# Revit family: Термостатический клапан HERZ-TS-90-E повышенной пропускной способности, угловой 7724
name_source: partatom
category: Rohrzubehör
revit_build: Autodesk Revit 2018 (Build: 20190510_1515(x64)
units: mm (PartAtom-declared; Revit-internal decimal feet)

## family parameters
Arbeitsebenenbasiert = Nein
Beim Laden mit Abzugskörper schneiden = Nein
Bemaßung runder Anschluss = Durchmesser verwenden
Gemeinsam genutzt = Nein
Immer vertikal = Ja
OmniClass-Nummer = 23.65.55.14
OmniClass-Titel = Valves for Liquid Services
Teiletyp = Unterbricht

## types (16) — shared parameters
H04 = 4.5 mm  [stored 0.0147638 ft]
H06 = 17 mm
H07 = 6.65 mm  [stored 0.0218176 ft]
Hersteller = HERZ Armaturen Ges.m.b.H.
L05 = 12.5 mm  [stored 0.0410105 ft]
R01 = 14 mm  [stored 0.0459318 ft]
R02 = 10.5 mm  [stored 0.0344488 ft]
R03 = 5.3 mm  [stored 0.0173885 ft]
R04 = 7 mm  [stored 0.0229659 ft]
R05 = 3 mm  [stored 0.00984252 ft]
R06 = 16.15 mm  [stored 0.0529856 ft]
S01 = 10 mm  [stored 0.0328084 ft]
S04 = 45 mm  [stored 0.147638 ft]
SCRNCODE = 05;00;02
SCRNSEQ = ARM;ARM_TYP="ALLF";2
URL = www.herz-armaturen.ru
Защитный колпачок = Пластик, серый
Исполнение = Универсальные модели со специальной муфтой для резьбовой трубы и компрессионных фитингов, никелированные, с белым защитным колпачком.
Корпус = Никелированная латунь
Макс. рабочая температура = 120 °C
Макс. рабочее давление = 1000000.0 Pa
Область применения = Одно- и двухтрубные системы водяного отопления.
Соединительная резьба для термостатической головки = M28x1.5
Среда = Качество воды в соответствии с ÖNORM H 5195 или директивой VDI 2035.

## per-type parameters (varying)
| type | TH_Kopf_7230 | TH_Kopf_7260 | TH_Kopf_9200_03 | TH_Kopf_9200_06 | TH_Kopf_9200_13 | TH_Kopf_9200_16 | TH_Kopf_9200_30 | TH_Kopf_9200_60 | TH_Kopf_9230 | TH_Kopf_9260 | TH_Kopf_9330_10000mm | TH_Kopf_9330_2000mm | TH_Kopf_9330_5000mm | TH_Kopf_9330_8000mm | TH_Kopf_9860 |
| С термостатической головкой_7230 | Ja | Nein | Nein | Nein | Nein | Nein | Nein | Nein | Nein | Nein | Nein | Nein | Nein | Nein | Nein |
| С термостатической головкой_7260 | Nein | Ja | Nein | Nein | Nein | Nein | Nein | Nein | Nein | Nein | Nein | Nein | Nein | Nein | Nein |
| С термостатической головкой_9200_03 | Nein | Nein | Ja | Nein | Nein | Nein | Nein | Nein | Nein | Nein | Nein | Nein | Nein | Nein | Nein |
| С термостатической головкой_9200_06 | Nein | Nein | Nein | Ja | Nein | Nein | Nein | Nein | Nein | Nein | Nein | Nein | Nein | Nein | Nein |
| С термостатической головкой_9200_13 | Nein | Nein | Nein | Nein | Ja | Nein | Nein | Nein | Nein | Nein | Nein | Nein | Nein | Nein | Nein |
| С термостатической головкой_9200_16 | Nein | Nein | Nein | Nein | Nein | Ja | Nein | Nein | Nein | Nein | Nein | Nein | Nein | Nein | Nein |
| С термостатической головкой_9200_30 | Nein | Nein | Nein | Nein | Nein | Nein | Ja | Nein | Nein | Nein | Nein | Nein | Nein | Nein | Nein |
| С термостатической головкой_9200_60 | Nein | Nein | Nein | Nein | Nein | Nein | Nein | Ja | Nein | Nein | Nein | Nein | Nein | Nein | Nein |
| С термостатической головкой_9230 | Nein | Nein | Nein | Nein | Nein | Nein | Nein | Nein | Ja | Nein | Nein | Nein | Nein | Nein | Nein |
| С термостатической головкой_9260 | Nein | Nein | Nein | Nein | Nein | Nein | Nein | Nein | Nein | Ja | Nein | Nein | Nein | Nein | Nein |
| С термостатической головкой_9330_10000мм | Nein | Nein | Nein | Nein | Nein | Nein | Nein | Nein | Nein | Nein | Ja | Nein | Nein | Nein | Nein |
| С термостатической головкой_9330_2000мм | Nein | Nein | Nein | Nein | Nein | Nein | Nein | Nein | Nein | Nein | Nein | Ja | Nein | Nein | Nein |
| С термостатической головкой_9330_5000мм | Nein | Nein | Nein | Nein | Nein | Nein | Nein | Nein | Nein | Nein | Nein | Nein | Ja | Nein | Nein |
| С термостатической головкой_9330_8000мм | Nein | Nein | Nein | Nein | Nein | Nein | Nein | Nein | Nein | Nein | Nein | Nein | Nein | Ja | Nein |
| Без термостатической головки | Nein | Nein | Nein | Nein | Nein | Nein | Nein | Nein | Nein | Nein | Nein | Nein | Nein | Nein | Nein |
| С термостатической головкой_9860 | Nein | Nein | Nein | Nein | Nein | Nein | Nein | Nein | Nein | Nein | Nein | Nein | Nein | Nein | Ja |

note: [stored X ft] marks values corroborated as IEEE doubles in the binary element streams (Revit-internal decimal feet)
